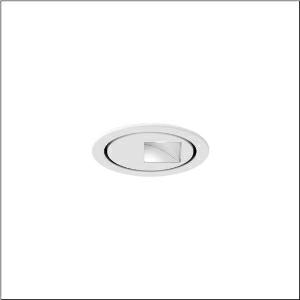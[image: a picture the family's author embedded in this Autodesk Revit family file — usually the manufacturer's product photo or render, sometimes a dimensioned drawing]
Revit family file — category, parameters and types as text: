
# Revit family: lunis_11_micro_round_51dj11b71wf21
name_source: partatom
category: Lighting Fixtures
units: mm (PartAtom-declared; Revit-internal decimal feet)

## family parameters
Cut with Voids When Loaded = No
Host = Face
Light Source = No
Part Type = Normal
Room Calculation Point = No
Round Connector Dimension = Use Diameter
Shared = No

## types (1)
- Lunis 11 micro round (1 x LED 3000K / CRI = 80 (unbekannt), 1320 lm, 3000K)
    Apparent Load = 20 VA
    CIE Flux Codes = 42 75 96 100 100
    Color Rendering = 80
    Color Temperature = 3000K
    Default Elevation = 1800 mm
    Description = Lunis 11 micro round, downlight, light control with wallwasher, of highly reflective aluminium, highly specular, light emission: direct distribution, LED rated luminous flux: 1.320lm, light colour: 830, with terminal, 3-pole, mains connection: 220..230V, AC, 50/60Hz, LED module, of aluminium, highly specular, white, diameter: 114mm, clamping range: 1..40mm, recessing ring, of plastic, traffic white (RAL 9016), protection rating (complete): IP20, insulation class (complete): insulation class II (safety insulation), certification: CE, permissible ambient temperature for indoor applications: 0..+35°C, packaging unit: 1 piece
    Height = 0 mm  [stored 0 ft]
    Lamp = 1 x LED 3000K / CRI >= 80 (unbekannt)
    Lamp Light Flux = 1320 lm
    Lamp count = 1
    Length = 114 mm
    Luminous efficacy = 67 lm/W
    Manufacturer = Siteco
    ModVariant = No
    Model = 51DJ11B71WF21
    Mounting Place = Ceiling
    Mounting Type = Recessed
    Number of Poles = 1
    OnlyDefault = Yes
    Power Factor = 1
    Product Name = Lunis 11 micro round
    Product group = downlight
    ProductGroupID = 401
    Protection Class = Protection class II
    Protection Degree = IP 20
    RLX_Detail_Level = 1
    RLX_Emergency_Light_Flux = 0 lm
    RLX_Emergency_Type = 0
    RLX_Emergency_Type_DB = No
    RlxData = <blob elided: 40853 chars, md5=8609ca57>
    Socket = socket
    Standby Power = 0 W
    System Light Flux = 1320 lm
    System Power = 20 W
    Type Comments = Product without accessories
    Type Image = l_1004773.jpg
    URL = http://relux.com
    VarID = ---
    Voltage = 0 V
    Weight = 0.00 kg
    Width = 114 mm

note: [stored X ft] marks values corroborated as IEEE doubles in the binary element streams (Revit-internal decimal feet)

## geometry (parser evidence)
native form markers: Blend x4, Sweep x10
no freeform markers — native parametric forms only
